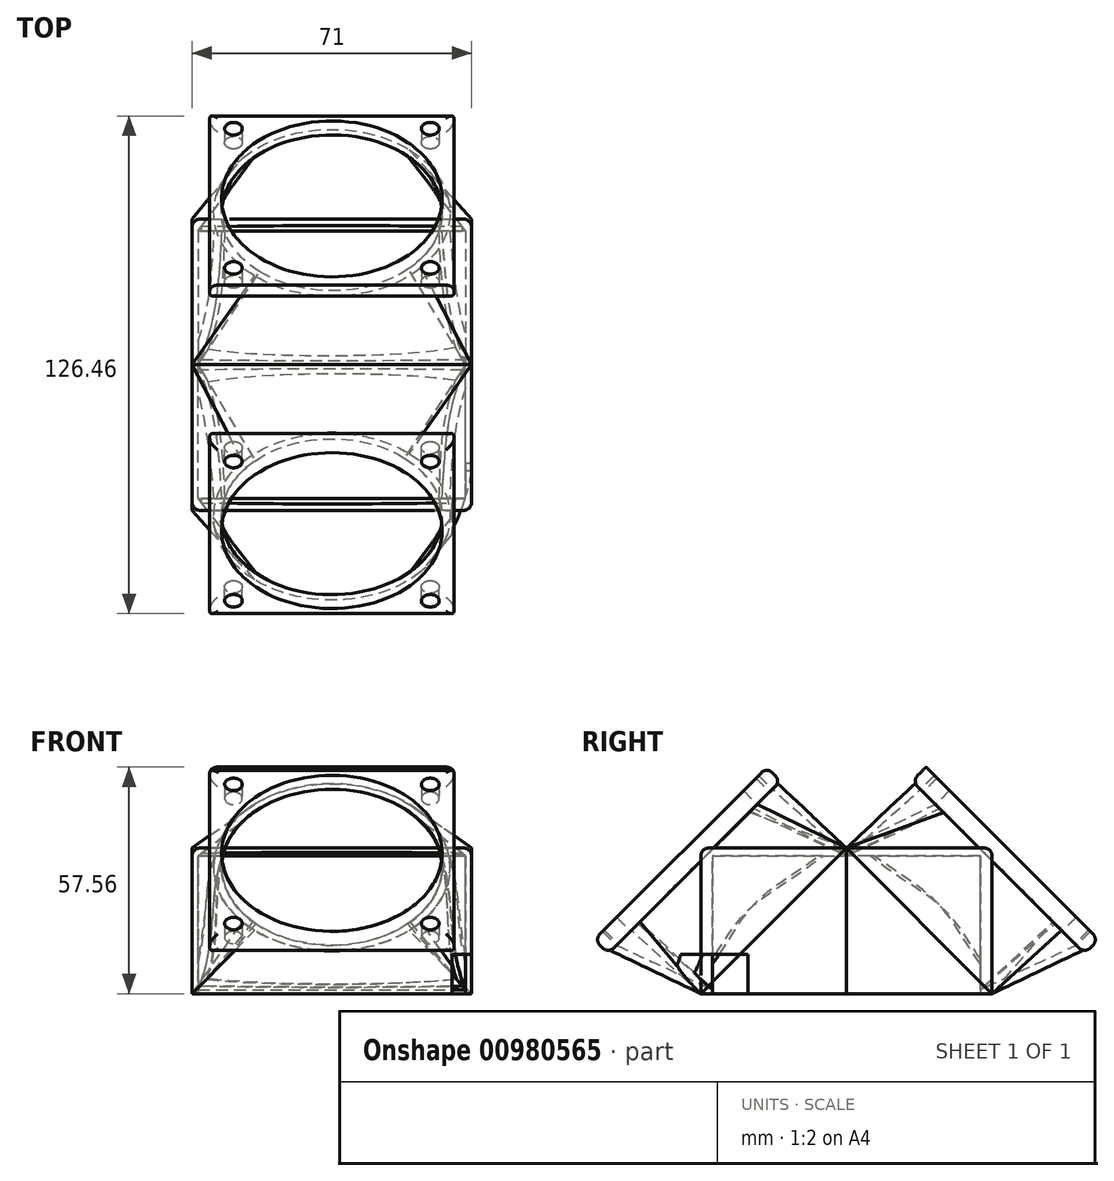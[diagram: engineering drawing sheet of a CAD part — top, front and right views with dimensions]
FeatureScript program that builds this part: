
annotation { "Feature Type Name" : "Feature", "Feature Type Description" : "" }
export const myFeature = defineFeature(function(context is Context, id is Id, definition is map)
    precondition{}
    {
        {
            var Q0;
            Q0=qCreatedBy(makeId("Front.planeOp"),FACE);
            var sketch = newSketch(context, id + "F0", { "sketchPlane" : qUnion([Q0])});
            skLineSegment(sketch, "E0.bottom", {"start": v(-34, 17.5) * mm, "end": v(34, 17.5) * mm});
            skLineSegment(sketch, "E0.top", {"start": v(-34, -17.5) * mm, "end": v(34, -17.5) * mm});
            skLineSegment(sketch, "E0.left", {"start": v(-34, 17.5) * mm, "end": v(-34, -17.5) * mm});
            skLineSegment(sketch, "E0.right", {"start": v(34, 17.5) * mm, "end": v(34, -17.5) * mm});
            skPoint(sketch, "E0.middle", {"position": v(0, 0) * mm});
            skSolve(sketch);
        }
        {
            var Q0;
            Q0=makeQuery(id+"F0.imprint","IMPRINT",FACE,{"disambiguationData":[TD([[makeQuery(id+"F0.imprint","IMPRINT",EDGE,{"derivedFrom":sQuery(id+"F0.wireOp",EDGE,"E0.bottom")}),-1.0]])]});
            extrude(context, id + "F1", {"entities" : qUnion([Q0]), "depth" : 34 * mm, "offsetDistance" : 25 * mm});
        }
        {
            var Q0;
            Q0=makeQuery(id+"F1.opExtrude","CAP_FACE",FACE,{"disambiguationData":[OSD([sQuery(id+"F0.wireOp",EDGE,"E0.bottom"),sQuery(id+"F0.wireOp",EDGE,"E0.top"),sQuery(id+"F0.wireOp",EDGE,"E0.left"),sQuery(id+"F0.wireOp",EDGE,"E0.right")])],"isStart":false});
            var sketch = newSketch(context, id + "F2", { "sketchPlane" : qUnion([Q0])});
            skLineSegment(sketch, "E1", {"start": v(-34, 0) * mm, "end": v(34, 0) * mm, "construction": true});
            skSolve(sketch);
        }
        {
            var Q0;
            Q0=sQuery(id+"F0.wireOp",EDGE,"E0.top");
            cPlane(context, id + "F3", {"entities" : qUnion([Q0]), "cplaneType" : CPlaneType.LINE_ANGLE, "offset" : 25 * mm, "angle" : 45 * degree, "oppositeDirection" : true, "width" : 150 * mm, "height" : 150 * mm});
        }
        {
            var Q0;
            Q0=sQuery(id+"F0.wireOp",EDGE,"E0.bottom");
            cPlane(context, id + "F4", {"entities" : qUnion([Q0]), "cplaneType" : CPlaneType.LINE_ANGLE, "offset" : 25 * mm, "angle" : 45 * degree, "oppositeDirection" : true, "width" : 150 * mm, "height" : 150 * mm});
        }
        {
            var Q0;
            Q0=qCreatedBy(id+"F4.planeOp",FACE);
            var sketch = newSketch(context, id + "F5", { "sketchPlane" : qUnion([Q0])});
            skLineSegment(sketch, "E2.bottom", {"start": v(-34, 12.37) * mm, "end": v(34, 12.37) * mm});
            skLineSegment(sketch, "E2.top", {"start": v(-34, -35.7) * mm, "end": v(34, -35.7) * mm});
            skLineSegment(sketch, "E2.left", {"start": v(-34, 12.37) * mm, "end": v(-34, -35.7) * mm});
            skLineSegment(sketch, "E2.right", {"start": v(34, 12.37) * mm, "end": v(34, -35.7) * mm});
            skSolve(sketch);
        }
        {
            var Q0;
            Q0=qCreatedBy(id+"F3.planeOp",FACE);
            cPlane(context, id + "F6", {"entities" : qUnion([Q0]), "cplaneType" : CPlaneType.OFFSET, "offset" : 50 * mm, "oppositeDirection" : true, "width" : 150 * mm, "height" : 150 * mm});
        }
        {
            var Q0;
            Q0=qCreatedBy(id+"F6.planeOp",FACE);
            var sketch = newSketch(context, id + "F7", { "sketchPlane" : qUnion([Q0])});
            skArc(sketch, "E3", {"start": v(19.5, 3.13) * mm, "mid": v(0.77, 11.02) * mm, "end": v(-18.36, 4.17) * mm});
            skArc(sketch, "E4", {"start": v(-18.36, 4.17) * mm, "mid": v(-27.98, -15.87) * mm, "end": v(-19.97, -36.6) * mm});
            skArc(sketch, "E5", {"start": v(-19.97, -36.6) * mm, "mid": v(-0.48, -44.97) * mm, "end": v(19.28, -37.27) * mm});
            skArc(sketch, "E6", {"start": v(19.28, -37.27) * mm, "mid": v(28, -17.12) * mm, "end": v(19.5, 3.13) * mm});
            skSolve(sketch);
        }
        {
            var Q0;
            Q0 = qSketchRegion(id + "F5", true);
            var Q1;
            Q1=makeQuery(id+"F7.imprint","IMPRINT",FACE,{"disambiguationData":[TD([[makeQuery(id+"F7.imprint","IMPRINT",EDGE,{"derivedFrom":sQuery(id+"F7.wireOp",EDGE,"E3")}),1.0]])]});
            loft(context, id + "F8", {"sheetProfilesArray" : [{ "sheetProfileEntities" : qUnion([Q0]) }, { "sheetProfileEntities" : qUnion([Q1]) }]});
        }
        {
            var Q0;
            Q0=makeQuery(id+"F0.imprint","IMPRINT",FACE,{"disambiguationData":[TD([[makeQuery(id+"F0.imprint","IMPRINT",EDGE,{"derivedFrom":sQuery(id+"F0.wireOp",EDGE,"E0.bottom")}),-1.0]])]});
            var sketch = newSketch(context, id + "F9", { "sketchPlane" : qUnion([Q0])});
            skLineSegment(sketch, "E7", {"start": v(0, 17.5) * mm, "end": v(0, -17.5) * mm, "construction": true});
            skSolve(sketch);
        }
        {
            var Q0;
            Q0=makeQuery(id+"F9.imprint","IMPRINT",FACE,{"disambiguationData":[TD([[makeQuery(id+"F9.imprint","IMPRINT",EDGE,{"derivedFrom":makeQuery(id+"F0.imprint","IMPRINT",EDGE,{"derivedFrom":sQuery(id+"F0.wireOp",EDGE,"E0.bottom")})}),-1.0]])]});
            var sketch = newSketch(context, id + "F10", { "sketchPlane" : qUnion([Q0])});
            skLineSegment(sketch, "E8.bottom", {"start": v(35.5, 19.5) * mm, "end": v(-35.5, 19.5) * mm});
            skLineSegment(sketch, "E8.top", {"start": v(35.5, -17.5) * mm, "end": v(-35.5, -17.5) * mm});
            skLineSegment(sketch, "E8.left", {"start": v(35.5, 19.5) * mm, "end": v(35.5, -17.5) * mm});
            skLineSegment(sketch, "E8.right", {"start": v(-35.5, 19.5) * mm, "end": v(-35.5, -17.5) * mm});
            skPoint(sketch, "E8.middle", {"position": v(0, 0) * mm});
            skSolve(sketch);
        }
        {
            var Q0;
            Q0 = qSketchRegion(id + "F10", true);
            extrude(context, id + "F11", {"entities" : qUnion([Q0]), "depth" : 37 * mm, "offsetDistance" : 25 * mm});
        }
        {
            var Q0;
            Q0=sQuery(id+"F10.wireOp",EDGE,"E8.bottom");
            cPlane(context, id + "F12", {"entities" : qUnion([Q0]), "cplaneType" : CPlaneType.LINE_ANGLE, "offset" : 25 * mm, "angle" : 45 * degree, "width" : 150 * mm, "height" : 150 * mm});
        }
        {
            var Q0;
            Q0=qCreatedBy(id+"F12.planeOp",FACE);
            var sketch = newSketch(context, id + "F13", { "sketchPlane" : qUnion([Q0])});
            skLineSegment(sketch, "E9.bottom", {"start": v(-35.5, 13.79) * mm, "end": v(35.5, 13.79) * mm});
            skLineSegment(sketch, "E9.top", {"start": v(-35.5, -38.54) * mm, "end": v(35.5, -38.54) * mm});
            skLineSegment(sketch, "E9.left", {"start": v(-35.5, 13.79) * mm, "end": v(-35.5, -38.54) * mm});
            skLineSegment(sketch, "E9.right", {"start": v(35.5, 13.79) * mm, "end": v(35.5, -38.54) * mm});
            skSolve(sketch);
        }
        {
            var Q0;
            Q0=qCreatedBy(id+"F6.planeOp",FACE);
            var sketch = newSketch(context, id + "F14", { "sketchPlane" : qUnion([Q0])});
            skCircle(sketch, "E10", {"center": v(0, -16.97) * mm, "radius": 30 * mm});
            skSolve(sketch);
        }
        {
            var Q0;
            Q0=qCreatedBy(id+"F6.planeOp",FACE);
            var sketch = newSketch(context, id + "F15", { "sketchPlane" : qUnion([Q0])});
            skLineSegment(sketch, "E11.bottom", {"start": v(-31, -47.97) * mm, "end": v(31, -47.97) * mm});
            skLineSegment(sketch, "E11.top", {"start": v(-31, 14.03) * mm, "end": v(31, 14.03) * mm});
            skLineSegment(sketch, "E11.left", {"start": v(-31, -47.97) * mm, "end": v(-31, 14.03) * mm});
            skLineSegment(sketch, "E11.right", {"start": v(31, -47.97) * mm, "end": v(31, 14.03) * mm});
            skPoint(sketch, "E11.middle", {"position": v(0, -16.97) * mm});
            skSolve(sketch);
        }
        {
            var Q0;
            Q0=qCreatedBy(id+"F6.planeOp",FACE);
            var sketch = newSketch(context, id + "F16", { "sketchPlane" : qUnion([Q0])});
            skLineSegment(sketch, "E12.bottom", {"start": v(-25, -42.18) * mm, "end": v(25, -42.18) * mm, "construction": true});
            skLineSegment(sketch, "E12.top", {"start": v(-25, 7.82) * mm, "end": v(25, 7.82) * mm, "construction": true});
            skLineSegment(sketch, "E12.left", {"start": v(-25, -42.18) * mm, "end": v(-25, 7.82) * mm, "construction": true});
            skLineSegment(sketch, "E12.right", {"start": v(25, -42.18) * mm, "end": v(25, 7.82) * mm, "construction": true});
            skPoint(sketch, "E12.middle", {"position": v(0, -17.18) * mm});
            skSolve(sketch);
        }
        {
            var Q0;
            Q0=qCreatedBy(id+"F6.planeOp",FACE);
            var sketch = newSketch(context, id + "F17", { "sketchPlane" : qUnion([Q0])});
            skCircle(sketch, "E13", {"center": v(25, -42.18) * mm, "radius": 2.25 * mm});
            skCircle(sketch, "E14", {"center": v(-25, -42.18) * mm, "radius": 2.25 * mm});
            skCircle(sketch, "E15", {"center": v(-25, 7.82) * mm, "radius": 2.25 * mm});
            skCircle(sketch, "E16", {"center": v(25, 7.82) * mm, "radius": 2.25 * mm});
            skSolve(sketch);
        }
        {
            var Q0;
            Q0=makeQuery(id+"F8.opLoft","CAP_FACE",FACE,{"disambiguationData":[OSD([makeQuery(id+"F7.imprint","IMPRINT",FACE,{"disambiguationData":[TD([[makeQuery(id+"F7.imprint","IMPRINT",EDGE,{"derivedFrom":sQuery(id+"F7.wireOp",EDGE,"E3")}),1.0]])]})])],"isStart":true});
            var Q1;
            Q1=makeQuery(id+"F17.imprint","IMPRINT",FACE,{"disambiguationData":[TD([[makeQuery(id+"F17.imprint","IMPRINT",EDGE,{"derivedFrom":sQuery(id+"F17.wireOp",EDGE,"E16")}),1.0]])]});
            var Q2;
            Q2=makeQuery(id+"F17.imprint","IMPRINT",FACE,{"disambiguationData":[TD([[makeQuery(id+"F17.imprint","IMPRINT",EDGE,{"derivedFrom":sQuery(id+"F17.wireOp",EDGE,"E15")}),1.0]])]});
            var Q3;
            Q3=makeQuery(id+"F17.imprint","IMPRINT",FACE,{"disambiguationData":[TD([[makeQuery(id+"F17.imprint","IMPRINT",EDGE,{"derivedFrom":sQuery(id+"F17.wireOp",EDGE,"E14")}),1.0]])]});
            var Q4;
            Q4=makeQuery(id+"F17.imprint","IMPRINT",FACE,{"disambiguationData":[TD([[makeQuery(id+"F17.imprint","IMPRINT",EDGE,{"derivedFrom":sQuery(id+"F17.wireOp",EDGE,"E13")}),1.0]])]});
            extrude(context, id + "F18", {"entities" : qUnion([Q0, Q1, Q2, Q3, Q4]), "depth" : 5 * mm, "offsetDistance" : 25 * mm});
        }
        {
            var Q0;
            Q0=makeQuery(id+"F13.imprint","IMPRINT",FACE,{"disambiguationData":[TD([[makeQuery(id+"F13.imprint","IMPRINT",EDGE,{"derivedFrom":sQuery(id+"F13.wireOp",EDGE,"E9.bottom")}),-1.0]])]});
            var Q1;
            Q1 = qSketchRegion(id + "F14", true);
            loft(context, id + "F19", {"sheetProfilesArray" : [{ "sheetProfileEntities" : qUnion([Q0]) }, { "sheetProfileEntities" : qUnion([Q1]) }]});
        }
        {
            var Q0;
            Q0=makeQuery(id+"F15.imprint","IMPRINT",FACE,{"disambiguationData":[TD([[makeQuery(id+"F15.imprint","IMPRINT",EDGE,{"derivedFrom":sQuery(id+"F15.wireOp",EDGE,"E11.bottom")}),1.0]])]});
            extrude(context, id + "F20", {"entities" : qUnion([Q0]), "oppositeDirection" : true, "depth" : 5 * mm, "offsetDistance" : 25 * mm});
        }
        {
            var Q0;
            Q0=makeQuery(id+"F18.opExtrude","SWEPT_BODY",BODY,{"disambiguationData":[OSD([sQuery(id+"F17.wireOp",EDGE,"E16")])]});
            var Q1;
            Q1=makeQuery(id+"F18.opExtrude","SWEPT_BODY",BODY,{"disambiguationData":[OSD([sQuery(id+"F17.wireOp",EDGE,"E15")])]});
            var Q2;
            Q2=makeQuery(id+"F18.opExtrude","SWEPT_BODY",BODY,{"disambiguationData":[OSD([sQuery(id+"F17.wireOp",EDGE,"E14")])]});
            var Q3;
            Q3=makeQuery(id+"F18.opExtrude","SWEPT_BODY",BODY,{"disambiguationData":[OSD([sQuery(id+"F17.wireOp",EDGE,"E13")])]});
            var Q4;
            Q4=makeQuery(id+"F18.opExtrude","SWEPT_BODY",BODY,{"disambiguationData":[OSD([makeQuery(id+"F7.imprint","IMPRINT",FACE,{"disambiguationData":[TD([[makeQuery(id+"F7.imprint","IMPRINT",EDGE,{"derivedFrom":sQuery(id+"F7.wireOp",EDGE,"E3")}),1.0]])]})])]});
            var Q5;
            Q5=makeQuery(id+"F8.opLoft","SWEPT_BODY",BODY,{"disambiguationData":[OSD([makeQuery(id+"F5.imprint","IMPRINT",FACE,{"disambiguationData":[TD([[makeQuery(id+"F5.imprint","IMPRINT",EDGE,{"derivedFrom":sQuery(id+"F5.wireOp",EDGE,"E2.bottom")}),-1.0]])]}),makeQuery(id+"F7.imprint","IMPRINT",FACE,{"disambiguationData":[TD([[makeQuery(id+"F7.imprint","IMPRINT",EDGE,{"derivedFrom":sQuery(id+"F7.wireOp",EDGE,"E3")}),1.0]])]})])]});
            var Q6;
            Q6=makeQuery(id+"F1.opExtrude","SWEPT_BODY",BODY,{"disambiguationData":[OSD([sQuery(id+"F0.wireOp",EDGE,"E0.bottom"),sQuery(id+"F0.wireOp",EDGE,"E0.top"),sQuery(id+"F0.wireOp",EDGE,"E0.left"),sQuery(id+"F0.wireOp",EDGE,"E0.right")])]});
            var Q7;
            Q7=makeQuery(id+"F11.opExtrude","SWEPT_BODY",BODY,{"disambiguationData":[OSD([sQuery(id+"F10.wireOp",EDGE,"E8.bottom"),sQuery(id+"F10.wireOp",EDGE,"E8.top"),sQuery(id+"F10.wireOp",EDGE,"E8.left"),sQuery(id+"F10.wireOp",EDGE,"E8.right")])]});
            var Q8;
            Q8=makeQuery(id+"F19.opLoft","SWEPT_BODY",BODY,{"disambiguationData":[OSD([makeQuery(id+"F13.imprint","IMPRINT",FACE,{"disambiguationData":[TD([[makeQuery(id+"F13.imprint","IMPRINT",EDGE,{"derivedFrom":sQuery(id+"F13.wireOp",EDGE,"E9.bottom")}),-1.0]])]}),makeQuery(id+"F14.imprint","IMPRINT",FACE,{"disambiguationData":[TD([[makeQuery(id+"F14.imprint","IMPRINT",EDGE,{"derivedFrom":sQuery(id+"F14.wireOp",EDGE,"E10")}),1.0]])]})])]});
            var Q9;
            Q9=makeQuery(id+"F20.opExtrude","SWEPT_BODY",BODY,{"disambiguationData":[OSD([sQuery(id+"F15.wireOp",EDGE,"E11.bottom"),sQuery(id+"F15.wireOp",EDGE,"E11.top"),sQuery(id+"F15.wireOp",EDGE,"E11.left"),sQuery(id+"F15.wireOp",EDGE,"E11.right")])]});
            booleanBodies(context, id + "F21", {"operationType" : BooleanOperationType.SUBTRACTION, "tools" : qUnion([Q0, Q1, Q2, Q3, Q4, Q5, Q6]), "targets" : qUnion([Q7, Q8, Q9])});
        }
        {
            var Q0;
            Q0=makeQuery(id+"F11.opExtrude","SWEPT_BODY",BODY,{"disambiguationData":[OSD([sQuery(id+"F10.wireOp",EDGE,"E8.bottom"),sQuery(id+"F10.wireOp",EDGE,"E8.top"),sQuery(id+"F10.wireOp",EDGE,"E8.left"),sQuery(id+"F10.wireOp",EDGE,"E8.right")])]});
            var Q1;
            Q1=sQuery(id+"F9.wireOp",EDGE,"E7");
            transform(context, id + "F22", {"entities" : qUnion([Q0]), "transformType" : TransformType.ROTATION, "transformAxis" : qUnion([Q1]), "angle" : 180 * degree, "makeCopy" : true});
        }
        {
            var Q0;
            Q0=makeQuery(id+"F19.opLoft","SWEPT_BODY",BODY,{"disambiguationData":[OSD([makeQuery(id+"F13.imprint","IMPRINT",FACE,{"disambiguationData":[TD([[makeQuery(id+"F13.imprint","IMPRINT",EDGE,{"derivedFrom":sQuery(id+"F13.wireOp",EDGE,"E9.bottom")}),-1.0]])]}),makeQuery(id+"F14.imprint","IMPRINT",FACE,{"disambiguationData":[TD([[makeQuery(id+"F14.imprint","IMPRINT",EDGE,{"derivedFrom":sQuery(id+"F14.wireOp",EDGE,"E10")}),1.0]])]})])]});
            var Q1;
            Q1=sQuery(id+"F9.wireOp",EDGE,"E7");
            transform(context, id + "F23", {"entities" : qUnion([Q0]), "transformType" : TransformType.ROTATION, "transformAxis" : qUnion([Q1]), "angle" : 180 * degree, "makeCopy" : true});
        }
        {
            var Q0;
            Q0=makeQuery(id+"F20.opExtrude","SWEPT_BODY",BODY,{"disambiguationData":[OSD([sQuery(id+"F15.wireOp",EDGE,"E11.bottom"),sQuery(id+"F15.wireOp",EDGE,"E11.top"),sQuery(id+"F15.wireOp",EDGE,"E11.left"),sQuery(id+"F15.wireOp",EDGE,"E11.right")])]});
            var Q1;
            Q1=sQuery(id+"F9.wireOp",EDGE,"E7");
            transform(context, id + "F24", {"entities" : qUnion([Q0]), "transformType" : TransformType.ROTATION, "transformAxis" : qUnion([Q1]), "angle" : 180 * degree, "makeCopy" : true});
        }
        {
            var Q0;
            Q0=makeQuery(id+"F20.opExtrude","CAP_EDGE",EDGE,{"disambiguationData":[OSD([sQuery(id+"F15.wireOp",EDGE,"E11.left")])],"isStart":false});
            var Q1;
            Q1=makeQuery(id+"F20.opExtrude","CAP_EDGE",EDGE,{"disambiguationData":[OSD([sQuery(id+"F15.wireOp",EDGE,"E11.top")])],"isStart":false});
            var Q2;
            Q2=makeQuery(id+"F20.opExtrude","CAP_EDGE",EDGE,{"disambiguationData":[OSD([sQuery(id+"F15.wireOp",EDGE,"E11.right")])],"isStart":false});
            var Q3;
            Q3=makeQuery(id+"F20.opExtrude","CAP_EDGE",EDGE,{"disambiguationData":[OSD([sQuery(id+"F15.wireOp",EDGE,"E11.bottom")])],"isStart":false});
            var Q4;
            Q4=makeQuery(id+"F20.opExtrude","CAP_EDGE",EDGE,{"disambiguationData":[OSD([sQuery(id+"F15.wireOp",EDGE,"E11.left")])],"isStart":true});
            var Q5;
            Q5=makeQuery(id+"F20.opExtrude","CAP_EDGE",EDGE,{"disambiguationData":[OSD([sQuery(id+"F15.wireOp",EDGE,"E11.bottom")])],"isStart":true});
            var Q6;
            Q6=makeQuery(id+"F20.opExtrude","CAP_EDGE",EDGE,{"disambiguationData":[OSD([sQuery(id+"F15.wireOp",EDGE,"E11.right")])],"isStart":true});
            var Q7;
            Q7=makeQuery(id+"F20.opExtrude","CAP_EDGE",EDGE,{"disambiguationData":[OSD([sQuery(id+"F15.wireOp",EDGE,"E11.top")])],"isStart":true});
            var Q8;
            Q8=makeQuery(id+"F11.opExtrude","CAP_EDGE",EDGE,{"disambiguationData":[OSD([sQuery(id+"F10.wireOp",EDGE,"E8.right")])],"isStart":false});
            var Q9;
            {var subQ0=sQuery(id+"F10.wireOp",EDGE,"E8.bottom");var subQ1=sQuery(id+"F10.wireOp",EDGE,"E8.right");Q9=makeQuery(id+"F21.opBoolean","SPLIT",EDGE,{"disambiguationData":[TD([makeQuery(id+"F11.opExtrude","SWEPT_FACE",FACE,{"disambiguationData":[OSD([subQ1])]})])],"derivedFrom":makeQuery(id+"F11.opExtrude","CAP_EDGE",EDGE,{"disambiguationData":[OSD([subQ0])],"isStart":false})});}
            var Q10;
            Q10=makeQuery(id+"F11.opExtrude","SWEPT_EDGE",EDGE,{"disambiguationData":[OSD([sQuery(id+"F10.wireOp",EDGE,"E8.bottom"),sQuery(id+"F10.wireOp",EDGE,"E8.right")])]});
            var Q11;
            Q11=makeQuery(id+"F11.opExtrude","CAP_EDGE",EDGE,{"disambiguationData":[OSD([sQuery(id+"F10.wireOp",EDGE,"E8.left")])],"isStart":false});
            var Q12;
            Q12=makeQuery(id+"F11.opExtrude","SWEPT_EDGE",EDGE,{"disambiguationData":[OSD([sQuery(id+"F10.wireOp",EDGE,"E8.bottom"),sQuery(id+"F10.wireOp",EDGE,"E8.left")])]});
            var Q13;
            {var subQ0=sQuery(id+"F10.wireOp",EDGE,"E8.bottom");var subQ1=sQuery(id+"F10.wireOp",EDGE,"E8.left");Q13=makeQuery(id+"F21.opBoolean","SPLIT",EDGE,{"disambiguationData":[TD([makeQuery(id+"F11.opExtrude","SWEPT_FACE",FACE,{"disambiguationData":[OSD([subQ1])]})])],"derivedFrom":makeQuery(id+"F11.opExtrude","CAP_EDGE",EDGE,{"disambiguationData":[OSD([subQ0])],"isStart":false})});}
            var Q14;
            Q14=makeQuery(id+"F22.opPattern","COPY",EDGE,{"derivedFrom":makeQuery(id+"F11.opExtrude","SWEPT_EDGE",EDGE,{"disambiguationData":[OSD([sQuery(id+"F10.wireOp",EDGE,"E8.bottom"),sQuery(id+"F10.wireOp",EDGE,"E8.right")])]}),"instanceName":"1"});
            var Q15;
            {var subQ0=sQuery(id+"F10.wireOp",EDGE,"E8.bottom");var subQ1=sQuery(id+"F10.wireOp",EDGE,"E8.right");Q15=makeQuery(id+"F22.opPattern","COPY",EDGE,{"derivedFrom":makeQuery(id+"F21.opBoolean","SPLIT",EDGE,{"disambiguationData":[TD([makeQuery(id+"F11.opExtrude","SWEPT_FACE",FACE,{"disambiguationData":[OSD([subQ1])]})])],"derivedFrom":makeQuery(id+"F11.opExtrude","CAP_EDGE",EDGE,{"disambiguationData":[OSD([subQ0])],"isStart":false})}),"instanceName":"1"});}
            var Q16;
            Q16=makeQuery(id+"F22.opPattern","COPY",EDGE,{"derivedFrom":makeQuery(id+"F11.opExtrude","CAP_EDGE",EDGE,{"disambiguationData":[OSD([sQuery(id+"F10.wireOp",EDGE,"E8.right")])],"isStart":false}),"instanceName":"1"});
            var Q17;
            Q17=makeQuery(id+"F24.opPattern","COPY",EDGE,{"derivedFrom":makeQuery(id+"F20.opExtrude","CAP_EDGE",EDGE,{"disambiguationData":[OSD([sQuery(id+"F15.wireOp",EDGE,"E11.right")])],"isStart":false}),"instanceName":"1"});
            var Q18;
            Q18=makeQuery(id+"F24.opPattern","COPY",EDGE,{"derivedFrom":makeQuery(id+"F20.opExtrude","CAP_EDGE",EDGE,{"disambiguationData":[OSD([sQuery(id+"F15.wireOp",EDGE,"E11.right")])],"isStart":true}),"instanceName":"1"});
            var Q19;
            Q19=makeQuery(id+"F24.opPattern","COPY",EDGE,{"derivedFrom":makeQuery(id+"F20.opExtrude","CAP_EDGE",EDGE,{"disambiguationData":[OSD([sQuery(id+"F15.wireOp",EDGE,"E11.top")])],"isStart":true}),"instanceName":"1"});
            var Q20;
            Q20=makeQuery(id+"F24.opPattern","COPY",EDGE,{"derivedFrom":makeQuery(id+"F20.opExtrude","CAP_EDGE",EDGE,{"disambiguationData":[OSD([sQuery(id+"F15.wireOp",EDGE,"E11.bottom")])],"isStart":true}),"instanceName":"1"});
            var Q21;
            Q21=makeQuery(id+"F24.opPattern","COPY",EDGE,{"derivedFrom":makeQuery(id+"F20.opExtrude","CAP_EDGE",EDGE,{"disambiguationData":[OSD([sQuery(id+"F15.wireOp",EDGE,"E11.bottom")])],"isStart":false}),"instanceName":"1"});
            var Q22;
            Q22=makeQuery(id+"F24.opPattern","COPY",EDGE,{"derivedFrom":makeQuery(id+"F20.opExtrude","CAP_EDGE",EDGE,{"disambiguationData":[OSD([sQuery(id+"F15.wireOp",EDGE,"E11.left")])],"isStart":false}),"instanceName":"1"});
            var Q23;
            Q23=makeQuery(id+"F24.opPattern","COPY",EDGE,{"derivedFrom":makeQuery(id+"F20.opExtrude","CAP_EDGE",EDGE,{"disambiguationData":[OSD([sQuery(id+"F15.wireOp",EDGE,"E11.left")])],"isStart":true}),"instanceName":"1"});
            var Q24;
            Q24=makeQuery(id+"F22.opPattern","COPY",EDGE,{"derivedFrom":makeQuery(id+"F11.opExtrude","CAP_EDGE",EDGE,{"disambiguationData":[OSD([sQuery(id+"F10.wireOp",EDGE,"E8.left")])],"isStart":false}),"instanceName":"1"});
            var Q25;
            {var subQ0=sQuery(id+"F10.wireOp",EDGE,"E8.bottom");var subQ1=sQuery(id+"F10.wireOp",EDGE,"E8.left");Q25=makeQuery(id+"F22.opPattern","COPY",EDGE,{"derivedFrom":makeQuery(id+"F21.opBoolean","SPLIT",EDGE,{"disambiguationData":[TD([makeQuery(id+"F11.opExtrude","SWEPT_FACE",FACE,{"disambiguationData":[OSD([subQ1])]})])],"derivedFrom":makeQuery(id+"F11.opExtrude","CAP_EDGE",EDGE,{"disambiguationData":[OSD([subQ0])],"isStart":false})}),"instanceName":"1"});}
            var Q26;
            Q26=makeQuery(id+"F22.opPattern","COPY",EDGE,{"derivedFrom":makeQuery(id+"F11.opExtrude","SWEPT_EDGE",EDGE,{"disambiguationData":[OSD([sQuery(id+"F10.wireOp",EDGE,"E8.bottom"),sQuery(id+"F10.wireOp",EDGE,"E8.left")])]}),"instanceName":"1"});
            fillet(context, id + "F25", {"entities" : qUnion([Q0, Q1, Q2, Q3, Q4, Q5, Q6, Q7, Q8, Q9, Q10, Q11, Q12, Q13, Q14, Q15, Q16, Q17, Q18, Q19, Q20, Q21, Q22, Q23, Q24, Q25, Q26]), "radius" : 2 * mm, "tangentPropagation" : true, "allowEdgeOverflow" : false});
        }
        {
            var Q0;
            Q0=makeQuery(id+"F11.opExtrude","SWEPT_FACE",FACE,{"disambiguationData":[OSD([sQuery(id+"F10.wireOp",EDGE,"E8.left")])]});
            var sketch = newSketch(context, id + "F26", { "sketchPlane" : qUnion([Q0])});
            skLineSegment(sketch, "E17.bottom", {"start": v(-25, -17.5) * mm, "end": v(-45, -17.5) * mm});
            skLineSegment(sketch, "E17.top", {"start": v(-25, -7.5) * mm, "end": v(-45, -7.5) * mm});
            skLineSegment(sketch, "E17.left", {"start": v(-25, -17.5) * mm, "end": v(-25, -7.5) * mm});
            skLineSegment(sketch, "E17.right", {"start": v(-45, -17.5) * mm, "end": v(-45, -7.5) * mm});
            skSolve(sketch);
        }
        {
            var Q0;
            Q0 = qSketchRegion(id + "F26", true);
            extrude(context, id + "F27", {"entities" : qUnion([Q0]), "oppositeDirection" : true, "depth" : 5 * mm, "offsetDistance" : 25 * mm});
        }
        {
            var Q0;
            Q0=makeQuery(id+"F27.opExtrude","SWEPT_BODY",BODY,{"disambiguationData":[OSD([sQuery(id+"F26.wireOp",EDGE,"E17.bottom"),sQuery(id+"F26.wireOp",EDGE,"E17.top"),sQuery(id+"F26.wireOp",EDGE,"E17.left"),sQuery(id+"F26.wireOp",EDGE,"E17.right")])]});
            var Q1;
            Q1=makeQuery(id+"F11.opExtrude","SWEPT_BODY",BODY,{"disambiguationData":[OSD([sQuery(id+"F10.wireOp",EDGE,"E8.bottom"),sQuery(id+"F10.wireOp",EDGE,"E8.top"),sQuery(id+"F10.wireOp",EDGE,"E8.left"),sQuery(id+"F10.wireOp",EDGE,"E8.right")])]});
            var Q2;
            Q2=makeQuery(id+"F19.opLoft","SWEPT_BODY",BODY,{"disambiguationData":[OSD([makeQuery(id+"F13.imprint","IMPRINT",FACE,{"disambiguationData":[TD([[makeQuery(id+"F13.imprint","IMPRINT",EDGE,{"derivedFrom":sQuery(id+"F13.wireOp",EDGE,"E9.bottom")}),-1.0]])]}),makeQuery(id+"F14.imprint","IMPRINT",FACE,{"disambiguationData":[TD([[makeQuery(id+"F14.imprint","IMPRINT",EDGE,{"derivedFrom":sQuery(id+"F14.wireOp",EDGE,"E10")}),1.0]])]})])]});
            booleanBodies(context, id + "F28", {"operationType" : BooleanOperationType.SUBTRACTION, "tools" : qUnion([Q0]), "targets" : qUnion([Q1, Q2])});
        }
    });
